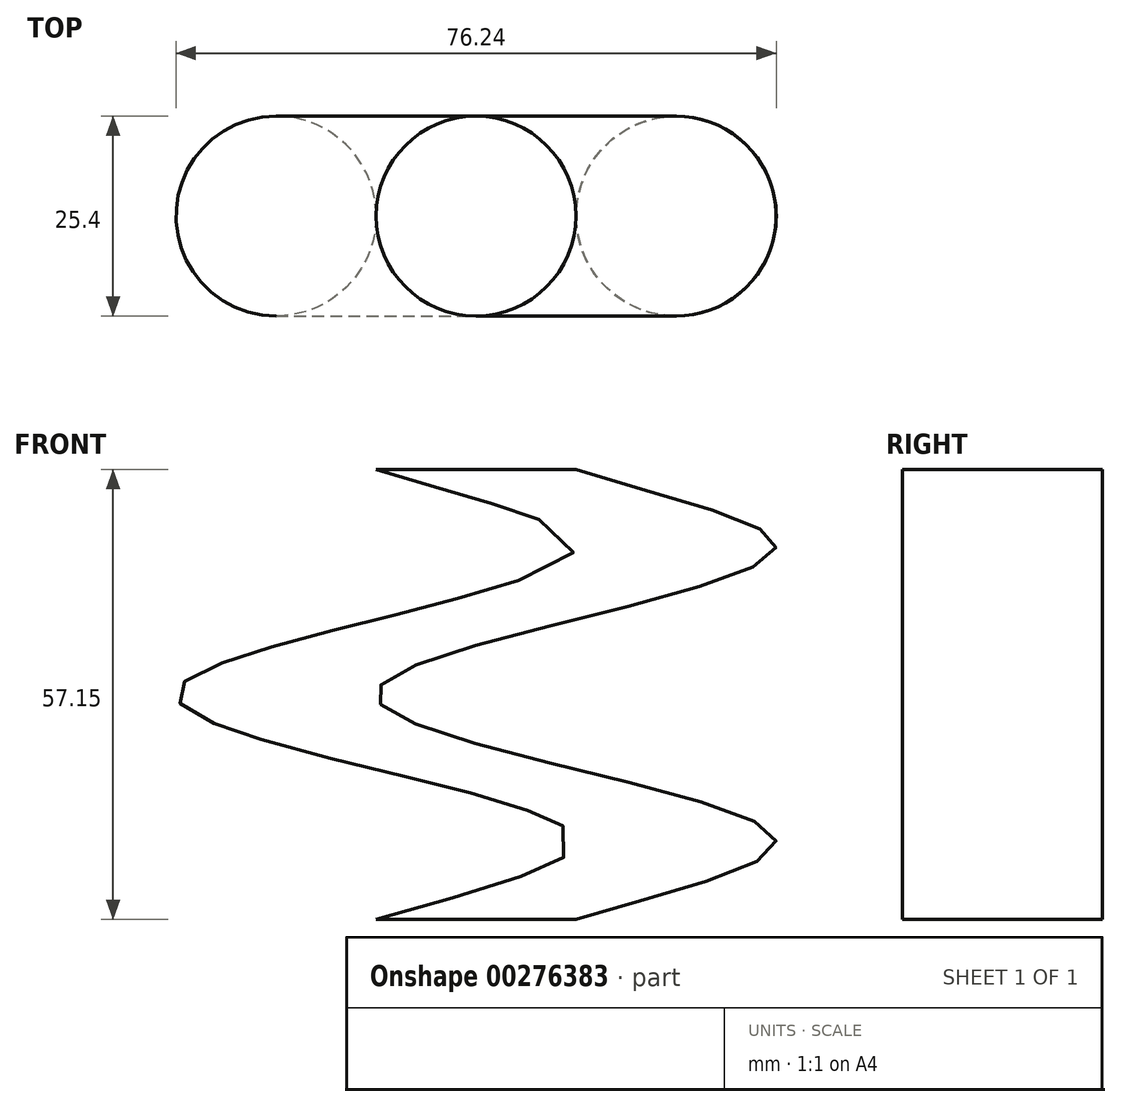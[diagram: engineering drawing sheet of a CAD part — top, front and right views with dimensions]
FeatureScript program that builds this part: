
annotation { "Feature Type Name" : "Feature", "Feature Type Description" : "" }
export const myFeature = defineFeature(function(context is Context, id is Id, definition is map)
    precondition{}
    {
        {
            var Q0;
            Q0=qCreatedBy(makeId("Top.planeOp"),FACE);
            var sketch = newSketch(context, id + "F0", { "sketchPlane" : qUnion([Q0])});
            skCircle(sketch, "E0", {"center": v(0, 0) * mm, "radius": 12.7 * mm});
            skSolve(sketch);
        }
        {
            var Q0;
            Q0=qCreatedBy(makeId("Front.planeOp"),FACE);
            var sketch = newSketch(context, id + "F1", { "sketchPlane" : qUnion([Q0])});
            skPoint(sketch, "E1.2.internal.orphan", {"position": v(0, 19.05) * mm});
            skPoint(sketch, "E1.4.internal.orphan", {"position": v(0, 38.1) * mm});
            skPoint(sketch, "E1.6.internal.orphan", {"position": v(0, 57.15) * mm});
            skPoint(sketch, "E1.start.orphan", {"position": v(0, 0) * mm});
            skFitSpline(sketch, "E2", {"points": [v(0, 0) * mm, v(25.4, 9.53) * mm, v(0, 19.05) * mm, v(-25.4, 28.58) * mm, v(0, 38.1) * mm, v(25.4, 47.63) * mm, v(0, 57.15) * mm], "startDerivative": vector(168.7, 51.2) * mm, "endDerivative": vector(-197.63, 63.67) * mm});
            skSolve(sketch);
        }
        {
            var Q0;
            Q0=makeQuery(id+"F0.imprint","IMPRINT",FACE,{"disambiguationData":[TD([[makeQuery(id+"F0.imprint","IMPRINT",EDGE,{"derivedFrom":sQuery(id+"F0.wireOp",EDGE,"E0")}),1.0]])]});
            var Q1;
            Q1=sQuery(id+"F1.wireOp",EDGE,"E2");
            sweep(context, id + "F2", {"profiles" : qUnion([Q0]), "path" : qUnion([Q1]), "keepProfileOrientation" : true});
        }
    });
